# Revit family: Pojemnik_na_papier_toaletowy JET S
name_source: partatom
category: Furniture
units: mm (PartAtom-declared; Revit-internal decimal feet)

## family parameters
Always vertical = Yes
Cut with Voids When Loaded = No
Host = Wall
Room Calculation Point = No
Shared = No

## types (1)
- Type 1
    Color / Kolor = Szary / Transparentny
    Depth / Glebokosc = 130 mm  [stored 0.426509 ft]
    Description = Pojemnik na papier toaletowy JET S jest naściennym, zamykanym na kluczyk dozownikiem, wykonanym z odpornego na uszkodzenia plastiku ABS. Transparentna obudowa ułatwia sprawdzanie aktualnego stanu wkładu wewnątrz pojemnika. Do modelu JET S pasuje rola o średnicy z przedziału 18 - 23 cm. Odrywanie poszczególnych kawałków papieru jest niezwykle proste dzięki ząbkowanej krawędzi w obudowie, co podnosi wygodę i higienę użytkowania. Pojemnik na papier toaletowy JET S jest gwarancją jakości i idealnie pasuje do różnorodnych toalet użytku publicznego, np. do szkół, hoteli, restauracji, biur czy gabinetów lekarskich.
    Height / Wysokosc = 260 mm  [stored 0.853018 ft]
    Manufacturer = FANECO.com
    Manufacturer code / Kod producenta = 5901764291954
    Material finish / Wykonczenie = Plastic ABS
    Model = JET S
    Product code / Kod produktu = J18PGWT
    Type Comments = Pojemnik na papier toaletowy JET S
    URL = https://faneco.com
    Weight / Waga = 0.6 kg
    Width / Szerokosc = 240 mm  [stored 0.787402 ft]

note: [stored X ft] marks values corroborated as IEEE doubles in the binary element streams (Revit-internal decimal feet)

## geometry (parser evidence)
native form markers: Extrusion x1, Sweep x8
no freeform markers — native parametric forms only
